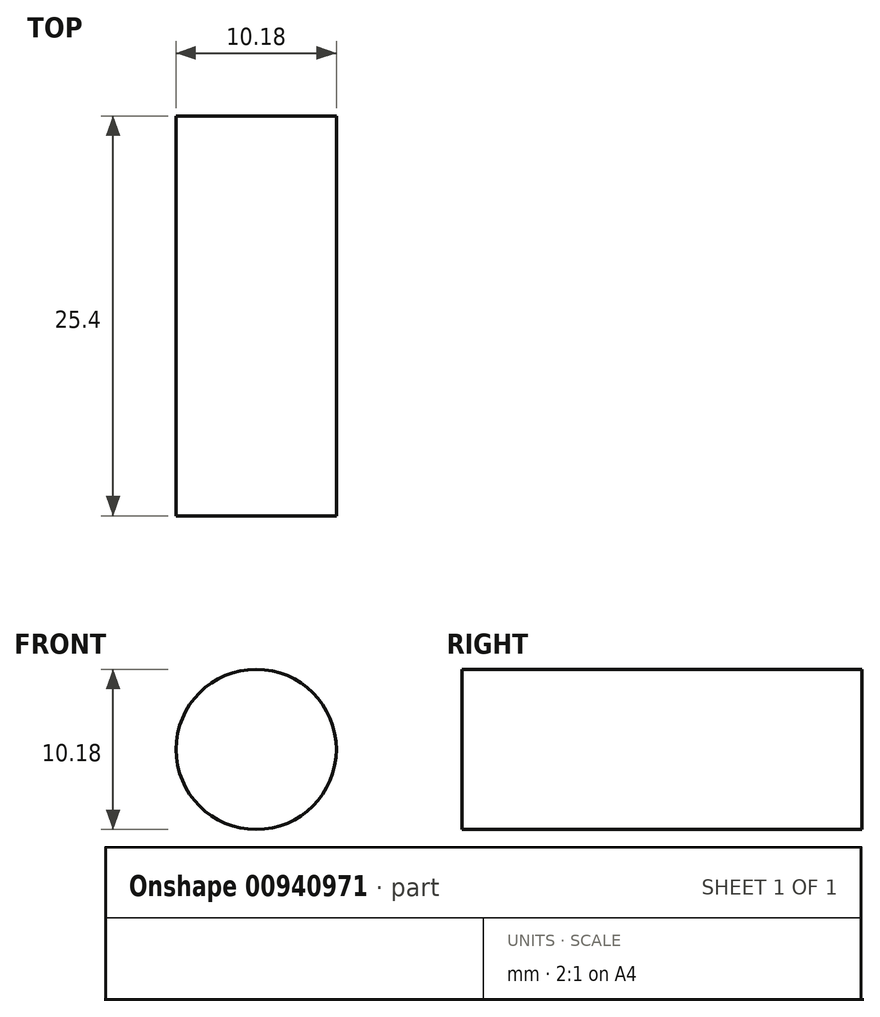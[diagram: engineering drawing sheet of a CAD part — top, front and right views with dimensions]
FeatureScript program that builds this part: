
annotation { "Feature Type Name" : "Feature", "Feature Type Description" : "" }
export const myFeature = defineFeature(function(context is Context, id is Id, definition is map)
    precondition{}
    {
        {
            var Q0;
            Q0=qCreatedBy(makeId("Front.planeOp"),FACE);
            var sketch = newSketch(context, id + "F0", { "sketchPlane" : qUnion([Q0])});
            skCircle(sketch, "E0", {"center": v(0, 0) * mm, "radius": 5.09 * mm});
            skSolve(sketch);
        }
        {
            var Q0;
            Q0 = qSketchRegion(id + "F0", true);
            extrude(context, id + "F1", {"entities" : qUnion([Q0]), "depth" : 25.4 * mm, "offsetDistance" : 25.4 * mm});
        }
    });
